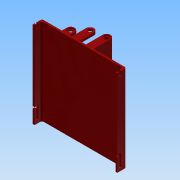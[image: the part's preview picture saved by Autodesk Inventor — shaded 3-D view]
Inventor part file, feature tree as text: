
AUTODESK INVENTOR PART (.ipt)
format: ipt  version: 2015 (Build 190159000, 159)  size: 343,040 bytes
history: native  units: mm
features: extrude x24, sketch x24, thread x6, fillet x5, chamfer x1
ambient origin geometry x8: Origin, YZ Plane, XZ Plane, XY Plane, X Axis, Y Axis, Z Axis, Center Point
bodies: 实体1 (feature_tree)
feature tree (60):
  extrude  "拉伸1"  Depth=10.0mm
  fillet  "圆角1"  Radius=10.0mm
  extrude  "拉伸2"  Depth=40.0mm
  fillet  "圆角2"  Radius=469.5mm
  extrude  "拉伸3"  Depth=42.0mm
  extrude  "拉伸4"  Depth=44.0mm
  extrude  "拉伸5"  Depth=64.0mm TaperAngle=0.0deg
  extrude  "拉伸6"  Depth=7.0mm
  fillet  "圆角3"  Radius=7.0mm
  extrude  "拉伸7"  Depth=3.0mm TaperAngle=0.0deg
  extrude  "拉伸8"  Depth=4.0mm TaperAngle=0.0deg
  extrude  "拉伸9"  Depth=14.0mm
  extrude  "拉伸10"  Depth=149.0mm
  extrude  "拉伸11"  Depth=21.0mm
  extrude  "拉伸12"  Depth=7.0mm TaperAngle=0.0deg
  extrude  "拉伸13"  Depth=3.0mm TaperAngle=0.0deg
  extrude  "拉伸14"  Depth=4.0mm TaperAngle=0.0deg
  thread  "螺纹1"  [1 undecoded]
  thread  "螺纹2"  [1 undecoded]
  extrude  "拉伸15"  Depth=246.5mm
  fillet  "圆角5"  Radius=91.384mm
  extrude  "拉伸16"  Depth=7.0mm TaperAngle=0.0deg
  extrude  "拉伸17"  Depth=2.0mm TaperAngle=0.0deg
  extrude  "拉伸18"  Depth=31.0mm
  extrude  "拉伸19"  Depth=5.0mm
  fillet  "圆角6"  Radius=5.0mm
  extrude  "拉伸20"  Depth=7.0mm
  extrude  "拉伸21"  Depth=7.0mm
  extrude  "拉伸22"  Depth=10.0mm TaperAngle=0.0deg
  extrude  "拉伸23"  Depth=42.0mm
  thread  "螺纹3"  [1 undecoded]
  thread  "螺纹4"  [1 undecoded]
  thread  "螺纹5"  [1 undecoded]
  thread  "螺纹6"  [1 undecoded]
  chamfer  "倒角1"  Distance=32.0mm
  extrude  "拉伸26"  Depth=7.0mm TaperAngle=0.0deg
  sketch  "草图1"  dims[d0=10.0mm d1=10.0mm d2=10.0mm]
  sketch  "草图2"  dims[d3=460.0mm d4=40.0mm d5=469.5mm d6=0.0mm]
  sketch  "草图3"  dims[d7=10.0mm d8=42.0mm]
  sketch  "草图4"  dims[d9=14.0mm d10=44.0mm]
  sketch  "草图5"  dims[d11=64.0mm d12=112.384mm d13=0.0mm]
  sketch  "草图6"  dims[d14=21.0mm d15=32.0mm d16=7.0mm d17=0.0mm]
  sketch  "草图7"  dims[d18=24.0mm d19=3.0mm d20=0.0mm]
  sketch  "草图8"  dims[d21=21.0mm d22=4.0mm d23=0.0mm]
  sketch  "草图9"  dims[d24=42.0mm d25=14.0mm]
  sketch  "草图10"  dims[d26=13.5mm d27=149.0mm]
  sketch  "草图12"  dims[d28=112.384mm d29=0.0mm d30=21.0mm]
  sketch  "草图13"  dims[d31=32.0mm d32=7.0mm d33=0.0mm]
  sketch  "草图14"  dims[d34=26.0mm d35=3.0mm d36=0.0mm]
  sketch  "草图15"  dims[d37=21.0mm d38=4.0mm d39=0.0mm d40=80.0mm d41=14.0mm]
  sketch  "草图16"  dims[d42=130.0mm d43=246.5mm d44=91.384mm d45=0.0mm]
  sketch  "草图17"  dims[d47=42.0mm d48=7.0mm d49=0.0mm]
  sketch  "草图18"  dims[d50=34.0mm d51=2.0mm d52=0.0mm]
  sketch  "草图19"  dims[d53=31.0mm d54=31.0mm]
  sketch  "草图20"  dims[d55=0.0mm d56=5.0mm d57=5.0mm]
  sketch  "草图23"  dims[d58=7.0mm d59=7.0mm]
  sketch  "草图24"  dims[d60=7.0mm d61=7.0mm]
  sketch  "草图25"  dims[d62=15.0mm d63=0.0mm d64=10.0mm d65=0.0mm]
  sketch  "草图26"  dims[d66=10.0mm d67=0.0mm d68=42.0mm d69=120.0mm d70=0.0mm d71=239.0mm d72=112.384mm d73=0.0mm]
  sketch  "草图28"  dims[d74=21.0mm d75=32.0mm d76=7.0mm d77=0.0mm d78=32.0mm d79=7.0mm d80=0.0mm d81=21.0mm d82=7.0mm d83=0.0mm d84=42.0mm d85=14.0mm d86=193.5mm d87=269.0mm d88=112.384mm d89=0.0mm d90=21.0mm d91=32.0mm d92=7.0mm d93=0.0mm d94=28.0mm d95=3.0mm d96=0.0mm d97=21.0mm d98=4.0mm d99=0.0mm d100=10.0mm d101=10.0mm d102=10.0mm d103=10.0mm d104=30.0mm d105=30.0mm d106=150.0mm d107=150.0mm d108=95.0mm d109=245.0mm d110=95.0mm d111=245.0mm d112=20.0mm d113=0.0mm d114=10.0mm d115=0.0mm d116=10.0mm d117=0.0mm d118=10.0mm d119=0.0mm d120=10.0mm d121=0.0mm d122=1.0mm d123=2.0mm d124=45.0deg d140=10.0mm d141=15.0mm d142=20.0mm d143=10.0mm d144=15.0mm d145=20.0mm d146=64.0mm d147=10.0mm d148=10.0mm d149=0.0mm]
note: 6 required parameter values undecoded (feature->parameter linkage not recoverable at this tier; creation-order binding heuristic only, values carry confidence <= 0.55)
